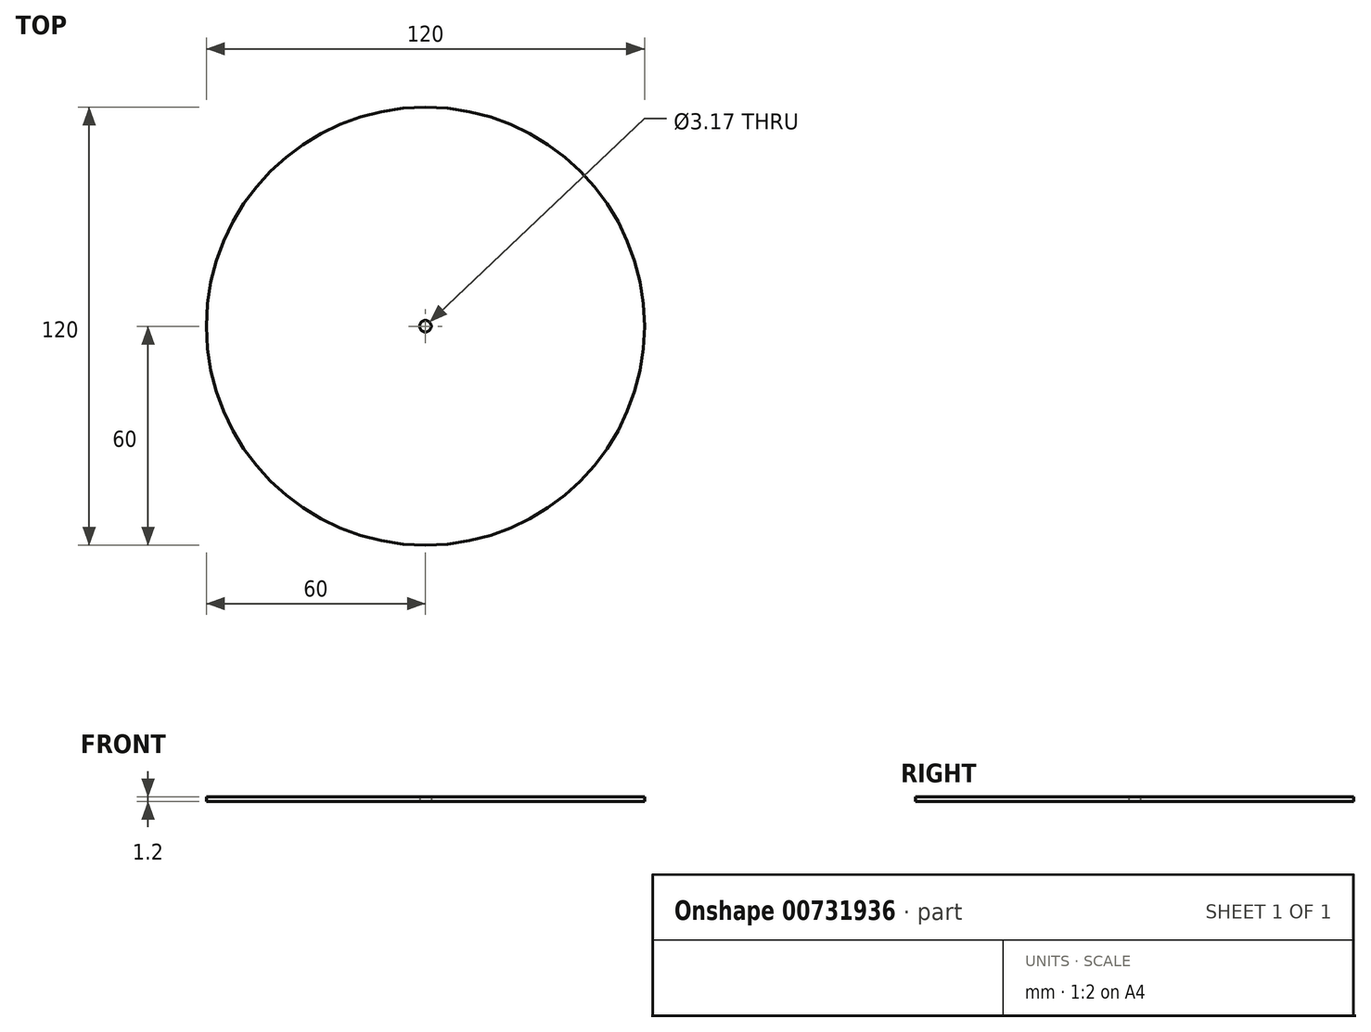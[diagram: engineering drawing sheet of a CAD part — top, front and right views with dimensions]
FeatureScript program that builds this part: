
annotation { "Feature Type Name" : "Feature", "Feature Type Description" : "" }
export const myFeature = defineFeature(function(context is Context, id is Id, definition is map)
    precondition{}
    {
        {
            var Q0;
            Q0=qCreatedBy(makeId("Top.planeOp"),FACE);
            var sketch = newSketch(context, id + "F0", { "sketchPlane" : qUnion([Q0])});
            skCircle(sketch, "E0", {"center": v(0, 0) * mm, "radius": 60 * mm});
            skCircle(sketch, "E1", {"center": v(0, 0) * mm, "radius": 1.59 * mm});
            skSolve(sketch);
        }
        {
            var Q0;
            Q0 = qSketchRegion(id + "F0", true);
            extrude(context, id + "F1", {"entities" : qUnion([Q0]), "depth" : 1.2 * mm, "offsetDistance" : 25.4 * mm});
        }
    });
